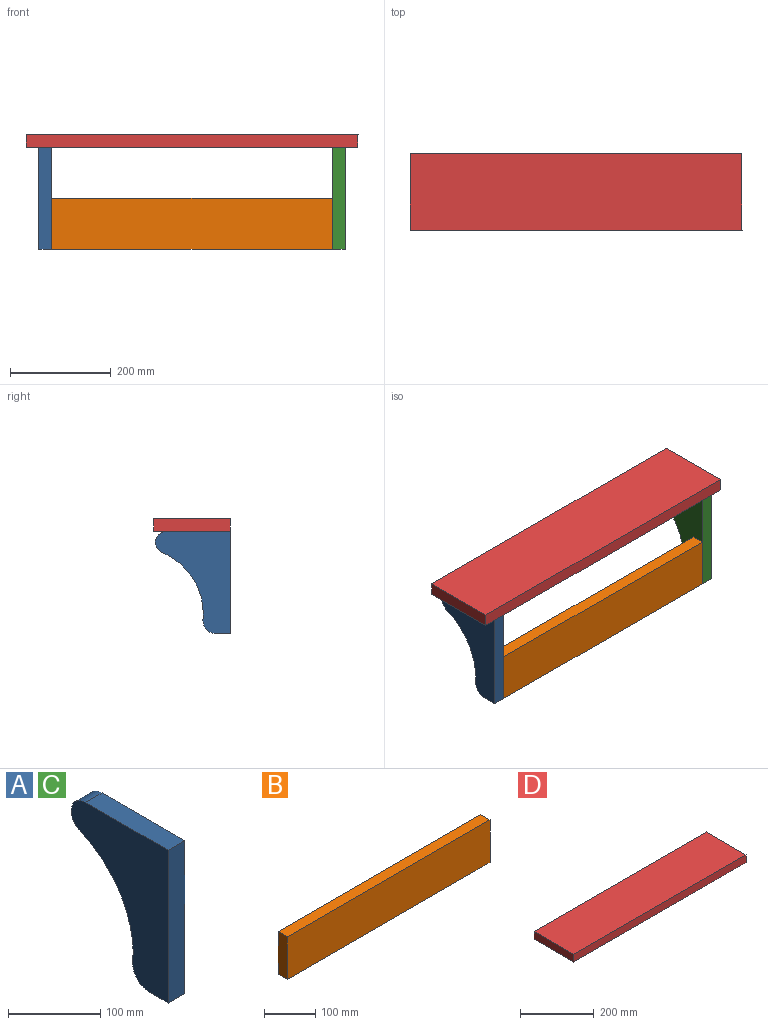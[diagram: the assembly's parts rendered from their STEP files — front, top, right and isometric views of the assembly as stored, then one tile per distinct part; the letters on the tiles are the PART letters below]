
ASSEMBLY  parts=4 mates=3
PART A: 9 faces, bbox 25.4x148.9x203.2 mm
  f0: plane 127x25.4mm, normal (0,0,1), area 3225.8mm2, adj f1,f6,f7,f8
  f1: plane 203.2x25.4mm, normal (0,-1,0), area 5161.3mm2, adj f0,f2,f7,f8
  f2: plane 29.07x25.4mm, normal (0,0,-1), area 738.3mm2, adj f1,f3,f7,f8
  f3: cylinder r=25.4mm len=28.01mm, axis (-1,0,0), area 1079.9mm2, adj f2,f4,f7,f8
  f4: cylinder r=132.08mm len=132.67mm, axis (-1,0,0), area 4210.6mm2, adj f3,f5,f7,f8
  f5: cylinder r=25.4mm len=25.4mm, axis (-1,0,0), area 12.3mm2, adj f4,f6,f7,f8
  f6: cylinder r=21.95mm len=42.33mm, axis (-1,0,0), area 1539.7mm2, adj f0,f5,f7,f8
  f7: plane 203.2x148.95mm, normal (1,0,0), area 17418.5mm2, adj f0,f1,f2,f3,f4,f5,f6
  f8: plane 203.2x148.95mm, normal (-1,0,0), area 17418.5mm2, adj f0,f1,f2,f3,f4,f5,f6
PART B: 6 faces, bbox 558.8x25.4x101.6 mm
  f0: plane 101.6x25.4mm, normal (1,0,0), area 2580.6mm2, adj f1,f3,f4,f5
  f1: plane 558.8x25.4mm, normal (0,0,1), area 14193.5mm2, adj f0,f2,f4,f5
  f2: plane 101.6x25.4mm, normal (-1,0,0), area 2580.6mm2, adj f1,f3,f4,f5
  f3: plane 558.8x25.4mm, normal (0,0,-1), area 14193.5mm2, adj f0,f2,f4,f5
  f4: plane 558.8x101.6mm, normal (0,-1,0), area 56774.1mm2, adj f0,f1,f2,f3
  f5: plane 558.8x101.6mm, normal (0,1,0), area 56774.1mm2, adj f0,f1,f2,f3
PART C: same geometry as A
PART D: 6 faces, bbox 660.4x152.4x25.4 mm
  f0: plane 152.4x25.4mm, normal (1,0,0), area 3871mm2, adj f1,f3,f4,f5
  f1: plane 660.4x25.4mm, normal (0,1,0), area 16774.2mm2, adj f0,f2,f4,f5
  f2: plane 152.4x25.4mm, normal (-1,0,0), area 3871mm2, adj f1,f3,f4,f5
  f3: plane 660.4x25.4mm, normal (0,-1,0), area 16774.2mm2, adj f0,f2,f4,f5
  f4: plane 660.4x152.4mm, normal (0,0,1), area 100645mm2, adj f0,f1,f2,f3
  f5: plane 660.4x152.4mm, normal (0,0,-1), area 100645mm2, adj f0,f1,f2,f3
PLACE A t=(-355.35,-85.07,138.72)mm
PLACE B rot(axis=(-0.1,0.15,0.98),0deg) t=(-50.55,-101.4,95.6)mm
PLACE C t=(228.85,-85.07,138.72)mm
PLACE D t=(-50.55,-50.6,248)mm
MATE fastened C.f0 <-> D.f5  axis (0,0,-1) through (254.25,-126.8,248)mm
MATE fastened B.f0 <-> C.f8  axis (1,0,0) through (228.85,-126.8,44.8)mm
MATE fastened A.f0 <-> D.f5  axis (0,0,1) through (-355.35,-126.8,248)mm
